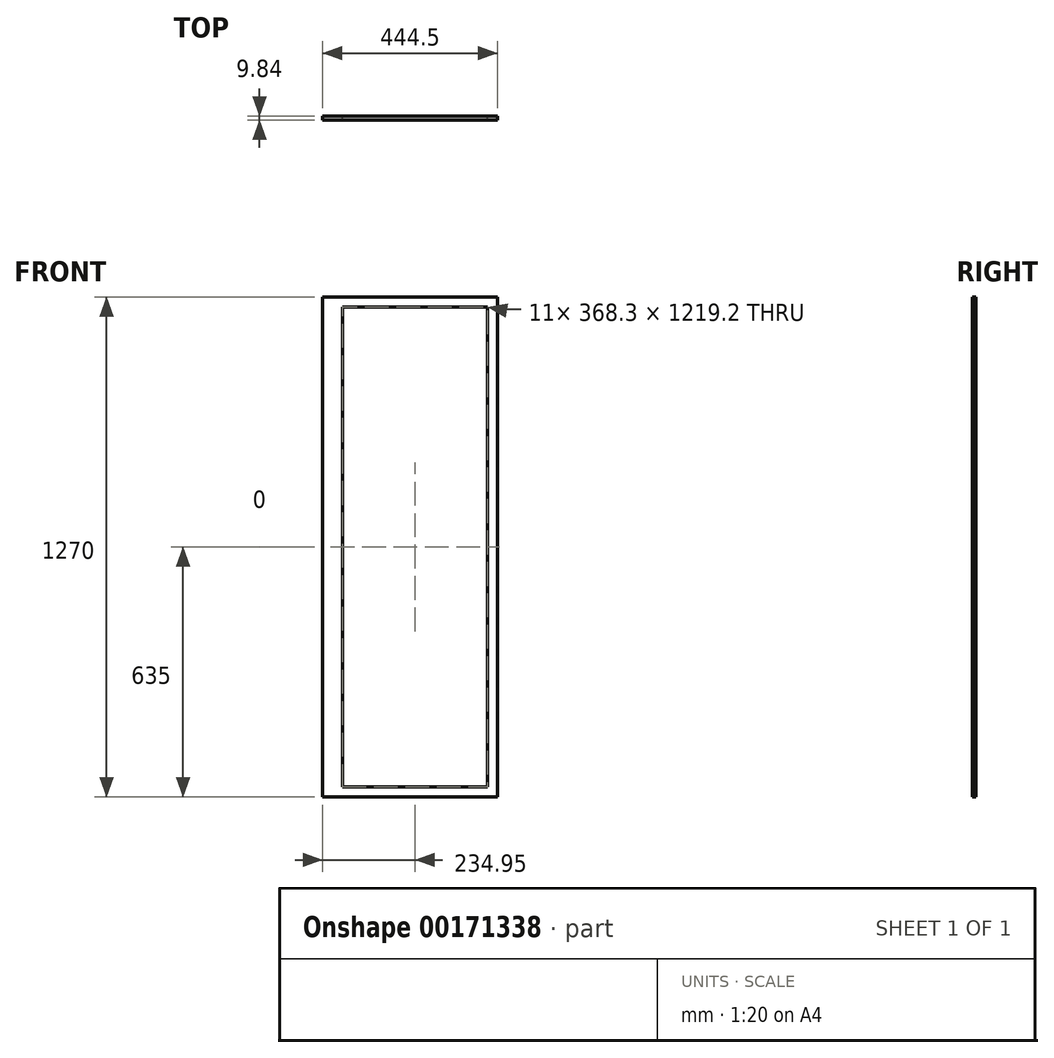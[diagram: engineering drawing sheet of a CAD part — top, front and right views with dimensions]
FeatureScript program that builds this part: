
annotation { "Feature Type Name" : "Feature", "Feature Type Description" : "" }
export const myFeature = defineFeature(function(context is Context, id is Id, definition is map)
    precondition{}
    {
        {
            var Q0;
            Q0=qCreatedBy(makeId("Front.planeOp"),FACE);
            var sketch = newSketch(context, id + "F0", { "sketchPlane" : qUnion([Q0])});
            skLineSegment(sketch, "E0.bottom", {"start": v(0, 0) * mm, "end": v(444.5, 0) * mm});
            skLineSegment(sketch, "E0.top", {"start": v(0, -1270) * mm, "end": v(444.5, -1270) * mm});
            skLineSegment(sketch, "E0.left", {"start": v(0, 0) * mm, "end": v(0, -1270) * mm});
            skLineSegment(sketch, "E0.right", {"start": v(444.5, 0) * mm, "end": v(444.5, -1270) * mm});
            skLineSegment(sketch, "E1.bottom", {"start": v(419.1, -1244.6) * mm, "end": v(50.8, -1244.6) * mm});
            skLineSegment(sketch, "E1.top", {"start": v(419.1, -25.4) * mm, "end": v(50.8, -25.4) * mm});
            skLineSegment(sketch, "E1.left", {"start": v(419.1, -1244.6) * mm, "end": v(419.1, -25.4) * mm});
            skLineSegment(sketch, "E1.right", {"start": v(50.8, -1244.6) * mm, "end": v(50.8, -25.4) * mm});
            skSolve(sketch);
        }
        {
            var Q0;
            Q0=makeQuery(id+"F0.imprint","IMPRINT",FACE,{"disambiguationData":[TD([[makeQuery(id+"F0.imprint","IMPRINT",EDGE,{"derivedFrom":sQuery(id+"F0.wireOp",EDGE,"E0.bottom")}),-1.0]])]});
            extrude(context, id + "F1", {"entities" : qUnion([Q0]), "depth" : 9.84 * mm});
        }
    });
